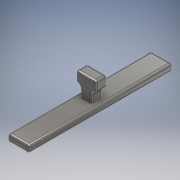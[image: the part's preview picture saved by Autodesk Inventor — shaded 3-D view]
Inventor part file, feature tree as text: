
AUTODESK INVENTOR PART (.ipt)
format: ipt  version: 2018 (Build 220112000, 112)  size: 179,200 bytes
history: native  units: mm
features: extrude x4, sketch x4, fillet x3
ambient origin geometry x8: Origin, YZ Plane, XZ Plane, XY Plane, X Axis, Y Axis, Z Axis, Center Point
bodies: Solid1 (feature_tree)
feature tree (11):
  extrude  "Extrusion1"  Depth=5.0mm
  extrude  "Extrusion2"  Depth=8.0mm
  extrude  "Extrusion3"  Depth=55.0mm
  extrude  "Extrusion4"  Depth=1.5mm
  fillet  "Fillet1"  Radius=8.0mm
  fillet  "Fillet2"  Radius=3.0mm
  fillet  "Fillet3"  Radius=7.0mm
  sketch  "Sketch1"  dims[d2=15.0mm d3=5.0mm]
  sketch  "Sketch2"  dims[d4=100.0mm d5=0.0mm d6=8.0mm]
  sketch  "Sketch3"  dims[d7=8.0mm d8=55.0mm]
  sketch  "Sketch4"  dims[d9=15.0mm d10=0.0mm d11=7.0mm d12=8.0mm d13=3.0mm d14=0.0mm d15=7.0mm d16=8.0mm d17=3.0mm d18=0.0mm d19=3.0mm d20=1.5mm d21=1.5mm]
